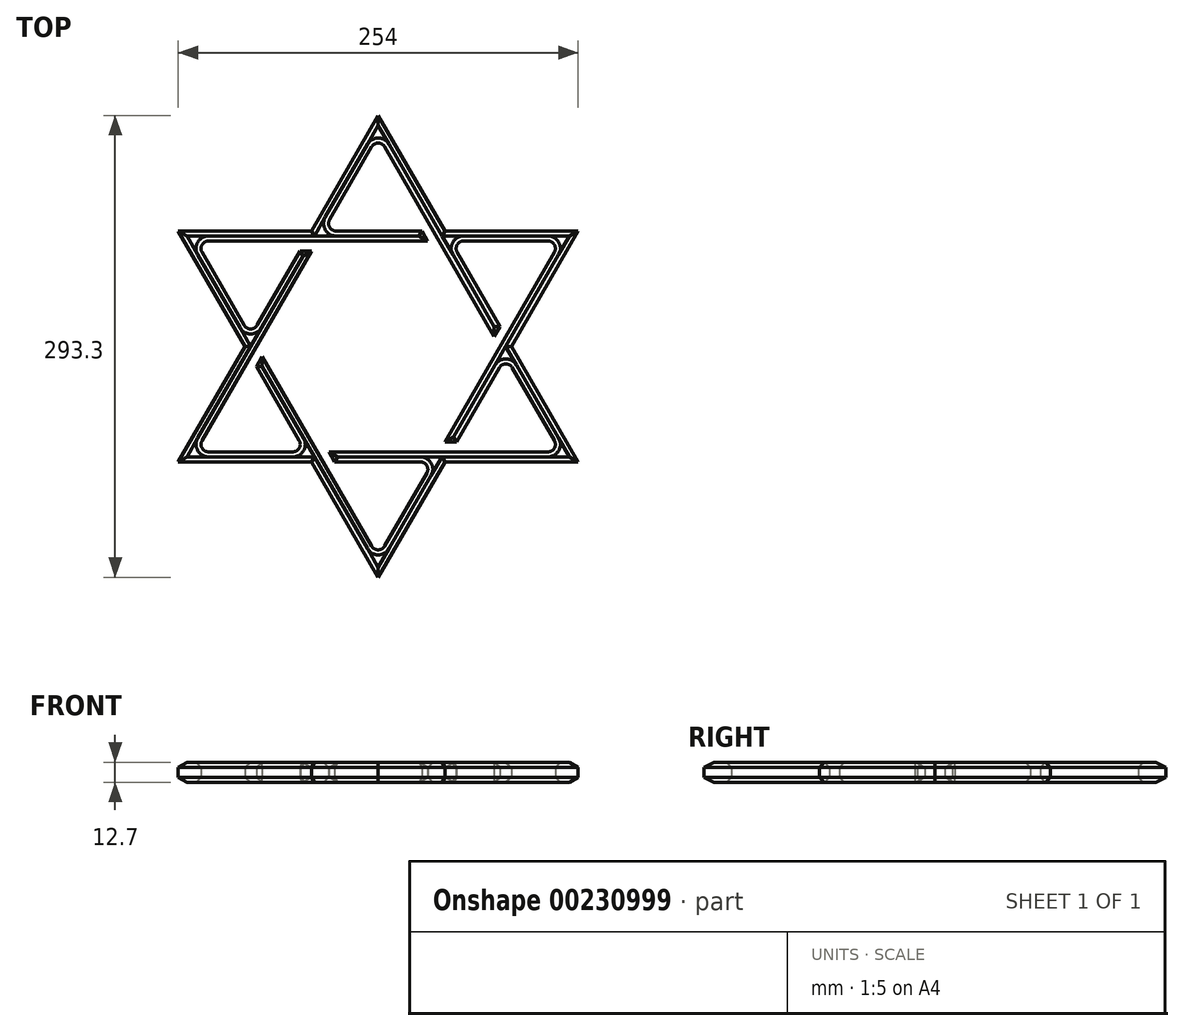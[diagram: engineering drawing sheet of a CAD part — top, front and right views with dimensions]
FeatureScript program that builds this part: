
annotation { "Feature Type Name" : "Feature", "Feature Type Description" : "" }
export const myFeature = defineFeature(function(context is Context, id is Id, definition is map)
    precondition{}
    {
        {
            var Q0;
            Q0=qCreatedBy(makeId("Top.planeOp"),FACE);
            var sketch = newSketch(context, id + "F0", { "sketchPlane" : qUnion([Q0])});
            skLineSegment(sketch, "E0", {"start": v(0, 146.65) * mm, "end": v(-42.33, 73.32) * mm});
            skLineSegment(sketch, "E1", {"start": v(-127, -73.32) * mm, "end": v(-42.33, -73.32) * mm});
            skLineSegment(sketch, "E2", {"start": v(0, 146.65) * mm, "end": v(42.33, 73.32) * mm});
            skLineSegment(sketch, "E3", {"start": v(127, 73.32) * mm, "end": v(84.67, 0) * mm});
            skLineSegment(sketch, "E4", {"start": v(0, -146.65) * mm, "end": v(-42.33, -73.32) * mm});
            skLineSegment(sketch, "E5", {"start": v(127, 73.32) * mm, "end": v(42.33, 73.32) * mm});
            skLineSegment(sketch, "E6.0", {"start": v(111.88, 59.83) * mm, "end": v(42.33, -60.62) * mm});
            skLineSegment(sketch, "E7.0", {"start": v(107.75, 66.97) * mm, "end": v(54.25, 66.97) * mm});
            skLineSegment(sketch, "E8.0", {"start": v(-4.12, -126.8) * mm, "end": v(-73.67, -6.35) * mm});
            skLineSegment(sketch, "E9.trimOffspring", {"start": v(-4.12, 126.8) * mm, "end": v(-30.88, 80.47) * mm});
            skLineSegment(sketch, "E10.trimOffspring", {"start": v(4.12, 126.8) * mm, "end": v(73.67, 6.35) * mm});
            skLineSegment(sketch, "E11.trimOffspring", {"start": v(-107.75, -66.97) * mm, "end": v(-54.25, -66.97) * mm});
            skLineSegment(sketch, "E12.0", {"start": v(-27.67, -73.32) * mm, "end": v(-31.33, -66.97) * mm});
            skLineSegment(sketch, "E13.trimOffspring", {"start": v(31.33, 66.97) * mm, "end": v(-107.75, 66.97) * mm});
            skLineSegment(sketch, "E14.trimOffspring", {"start": v(27.67, 73.32) * mm, "end": v(-26.75, 73.32) * mm});
            skLineSegment(sketch, "E15.trimOffspring", {"start": v(84.67, 0) * mm, "end": v(127, -73.32) * mm});
            skLineSegment(sketch, "E16.trimOffspring", {"start": v(77.33, 12.7) * mm, "end": v(73.67, 6.35) * mm});
            skLineSegment(sketch, "E17.trimOffspring", {"start": v(85.12, -13.5) * mm, "end": v(111.88, -59.83) * mm});
            skLineSegment(sketch, "E18.trimOffspring", {"start": v(42.33, -73.32) * mm, "end": v(0, -146.65) * mm});
            skLineSegment(sketch, "E19.trimOffspring", {"start": v(30.88, -80.47) * mm, "end": v(4.12, -126.8) * mm});
            skLineSegment(sketch, "E20.trimOffspring", {"start": v(42.33, -60.62) * mm, "end": v(49.67, -60.62) * mm});
            skLineSegment(sketch, "E21.trimOffspring", {"start": v(-27.67, -73.32) * mm, "end": v(26.75, -73.32) * mm});
            skLineSegment(sketch, "E22.trimOffspring", {"start": v(-31.33, -66.97) * mm, "end": v(107.75, -66.97) * mm});
            skLineSegment(sketch, "E23.trimOffspring", {"start": v(-84.67, 0) * mm, "end": v(-127, 73.32) * mm});
            skLineSegment(sketch, "E24.trimOffspring", {"start": v(-85.12, 13.5) * mm, "end": v(-111.88, 59.83) * mm});
            skLineSegment(sketch, "E25.trimOffspring", {"start": v(-73.67, -6.35) * mm, "end": v(-77.33, -12.7) * mm});
            skLineSegment(sketch, "E26.trimOffspring", {"start": v(-42.33, 60.62) * mm, "end": v(-111.88, -59.83) * mm});
            skLineSegment(sketch, "E27.trimOffspring", {"start": v(-49.67, 60.62) * mm, "end": v(-76.88, 13.5) * mm});
            skLineSegment(sketch, "E28.trimOffspring", {"start": v(-42.33, 60.62) * mm, "end": v(-49.67, 60.62) * mm});
            skLineSegment(sketch, "E29.trimOffspring", {"start": v(27.67, 73.32) * mm, "end": v(31.33, 66.97) * mm});
            skLineSegment(sketch, "E30.trimOffspring", {"start": v(-42.33, 73.32) * mm, "end": v(-127, 73.32) * mm});
            skLineSegment(sketch, "E31.trimOffspring", {"start": v(50.12, 59.83) * mm, "end": v(77.33, 12.7) * mm});
            skLineSegment(sketch, "E32.trimOffspring", {"start": v(76.88, -13.5) * mm, "end": v(49.67, -60.62) * mm});
            skLineSegment(sketch, "E33.trimOffspring", {"start": v(42.33, -73.32) * mm, "end": v(127, -73.32) * mm});
            skLineSegment(sketch, "E34.trimOffspring", {"start": v(-84.67, 0) * mm, "end": v(-127, -73.32) * mm});
            skLineSegment(sketch, "E35.trimOffspring", {"start": v(-50.12, -59.83) * mm, "end": v(-77.33, -12.7) * mm});
            skPoint(sketch, "E36.visualSharp", {"position": v(-116, 66.97) * mm});
            skArc(sketch, "E36.filletArc", {"start": v(-107.75, 66.97) * mm, "mid": v(-111.88, 64.6) * mm, "end": v(-111.88, 59.83) * mm});
            skPoint(sketch, "E37.visualSharp", {"position": v(0, 133.95) * mm});
            skArc(sketch, "E37.filletArc", {"start": v(4.12, 126.8) * mm, "mid": v(0, 129.18) * mm, "end": v(-4.12, 126.8) * mm});
            skPoint(sketch, "E38.visualSharp", {"position": v(-35, 73.32) * mm});
            skArc(sketch, "E38.filletArc", {"start": v(-30.88, 80.47) * mm, "mid": v(-30.88, 75.7) * mm, "end": v(-26.75, 73.32) * mm});
            skPoint(sketch, "E39.visualSharp", {"position": v(46, 66.97) * mm});
            skArc(sketch, "E39.filletArc", {"start": v(54.25, 66.97) * mm, "mid": v(50.12, 64.6) * mm, "end": v(50.12, 59.83) * mm});
            skPoint(sketch, "E40.visualSharp", {"position": v(116, 66.97) * mm});
            skArc(sketch, "E40.filletArc", {"start": v(111.88, 59.83) * mm, "mid": v(111.88, 64.6) * mm, "end": v(107.75, 66.97) * mm});
            skPoint(sketch, "E41.visualSharp", {"position": v(116, -66.97) * mm});
            skArc(sketch, "E41.filletArc", {"start": v(107.75, -66.97) * mm, "mid": v(111.88, -64.6) * mm, "end": v(111.88, -59.83) * mm});
            skPoint(sketch, "E42.visualSharp", {"position": v(81, -6.35) * mm});
            skArc(sketch, "E42.filletArc", {"start": v(85.12, -13.5) * mm, "mid": v(81, -11.11) * mm, "end": v(76.88, -13.5) * mm});
            skPoint(sketch, "E43.visualSharp", {"position": v(0, -133.95) * mm});
            skArc(sketch, "E43.filletArc", {"start": v(-4.12, -126.8) * mm, "mid": v(0, -129.18) * mm, "end": v(4.12, -126.8) * mm});
            skPoint(sketch, "E44.visualSharp", {"position": v(35, -73.32) * mm});
            skArc(sketch, "E44.filletArc", {"start": v(30.88, -80.47) * mm, "mid": v(30.88, -75.7) * mm, "end": v(26.75, -73.32) * mm});
            skPoint(sketch, "E45.visualSharp", {"position": v(-116, -66.97) * mm});
            skArc(sketch, "E45.filletArc", {"start": v(-111.88, -59.83) * mm, "mid": v(-111.88, -64.6) * mm, "end": v(-107.75, -66.97) * mm});
            skPoint(sketch, "E46.visualSharp", {"position": v(-81, 6.35) * mm});
            skArc(sketch, "E46.filletArc", {"start": v(-85.12, 13.5) * mm, "mid": v(-81, 11.11) * mm, "end": v(-76.88, 13.5) * mm});
            skPoint(sketch, "E47.visualSharp", {"position": v(-46, -66.97) * mm});
            skArc(sketch, "E47.filletArc", {"start": v(-54.25, -66.97) * mm, "mid": v(-50.12, -64.6) * mm, "end": v(-50.12, -59.83) * mm});
            skSolve(sketch);
        }
        {
            var Q0;
            Q0=makeQuery(id+"F0.imprint","IMPRINT",FACE,{"disambiguationData":[TD([[makeQuery(id+"F0.imprint","IMPRINT",EDGE,{"derivedFrom":sQuery(id+"F0.wireOp",EDGE,"E0")}),1.0]])]});
            extrude(context, id + "F1", {"entities" : qUnion([Q0]), "depth" : 12.7 * mm});
        }
        {
            var Q0;
            Q0=makeQuery(id+"F1.opExtrude","CAP_FACE",FACE,{"disambiguationData":[OSD([sQuery(id+"F0.wireOp",EDGE,"E0"),sQuery(id+"F0.wireOp",EDGE,"E1"),sQuery(id+"F0.wireOp",EDGE,"E2"),sQuery(id+"F0.wireOp",EDGE,"E3"),sQuery(id+"F0.wireOp",EDGE,"E4"),sQuery(id+"F0.wireOp",EDGE,"E5"),sQuery(id+"F0.wireOp",EDGE,"E6.0"),sQuery(id+"F0.wireOp",EDGE,"E7.0"),sQuery(id+"F0.wireOp",EDGE,"E8.0"),sQuery(id+"F0.wireOp",EDGE,"E9.trimOffspring"),sQuery(id+"F0.wireOp",EDGE,"E10.trimOffspring"),sQuery(id+"F0.wireOp",EDGE,"E11.trimOffspring"),sQuery(id+"F0.wireOp",EDGE,"E12.0"),sQuery(id+"F0.wireOp",EDGE,"E13.trimOffspring"),sQuery(id+"F0.wireOp",EDGE,"E14.trimOffspring"),sQuery(id+"F0.wireOp",EDGE,"E15.trimOffspring"),sQuery(id+"F0.wireOp",EDGE,"E16.trimOffspring"),sQuery(id+"F0.wireOp",EDGE,"E17.trimOffspring"),sQuery(id+"F0.wireOp",EDGE,"E18.trimOffspring"),sQuery(id+"F0.wireOp",EDGE,"E19.trimOffspring"),sQuery(id+"F0.wireOp",EDGE,"E20.trimOffspring"),sQuery(id+"F0.wireOp",EDGE,"E21.trimOffspring"),sQuery(id+"F0.wireOp",EDGE,"E22.trimOffspring"),sQuery(id+"F0.wireOp",EDGE,"E23.trimOffspring"),sQuery(id+"F0.wireOp",EDGE,"E24.trimOffspring"),sQuery(id+"F0.wireOp",EDGE,"E25.trimOffspring"),sQuery(id+"F0.wireOp",EDGE,"E26.trimOffspring"),sQuery(id+"F0.wireOp",EDGE,"E27.trimOffspring"),sQuery(id+"F0.wireOp",EDGE,"E28.trimOffspring"),sQuery(id+"F0.wireOp",EDGE,"E29.trimOffspring"),sQuery(id+"F0.wireOp",EDGE,"E30.trimOffspring"),sQuery(id+"F0.wireOp",EDGE,"E31.trimOffspring"),sQuery(id+"F0.wireOp",EDGE,"E32.trimOffspring"),sQuery(id+"F0.wireOp",EDGE,"E33.trimOffspring"),sQuery(id+"F0.wireOp",EDGE,"E34.trimOffspring"),sQuery(id+"F0.wireOp",EDGE,"E35.trimOffspring"),sQuery(id+"F0.wireOp",EDGE,"E36.filletArc"),sQuery(id+"F0.wireOp",EDGE,"E37.filletArc"),sQuery(id+"F0.wireOp",EDGE,"E38.filletArc"),sQuery(id+"F0.wireOp",EDGE,"E39.filletArc"),sQuery(id+"F0.wireOp",EDGE,"E40.filletArc"),sQuery(id+"F0.wireOp",EDGE,"E41.filletArc"),sQuery(id+"F0.wireOp",EDGE,"E42.filletArc"),sQuery(id+"F0.wireOp",EDGE,"E43.filletArc"),sQuery(id+"F0.wireOp",EDGE,"E44.filletArc"),sQuery(id+"F0.wireOp",EDGE,"E45.filletArc"),sQuery(id+"F0.wireOp",EDGE,"E46.filletArc"),sQuery(id+"F0.wireOp",EDGE,"E47.filletArc")])],"isStart":false});
            chamfer(context, id + "F2", {"entities" : qUnion([Q0]), "width" : 3.17 * mm, "tangentPropagation" : true});
        }
        {
            var Q0;
            Q0=makeQuery(id+"F1.opExtrude","CAP_FACE",FACE,{"disambiguationData":[OSD([sQuery(id+"F0.wireOp",EDGE,"E0"),sQuery(id+"F0.wireOp",EDGE,"E1"),sQuery(id+"F0.wireOp",EDGE,"E2"),sQuery(id+"F0.wireOp",EDGE,"E3"),sQuery(id+"F0.wireOp",EDGE,"E4"),sQuery(id+"F0.wireOp",EDGE,"E5"),sQuery(id+"F0.wireOp",EDGE,"E6.0"),sQuery(id+"F0.wireOp",EDGE,"E7.0"),sQuery(id+"F0.wireOp",EDGE,"E8.0"),sQuery(id+"F0.wireOp",EDGE,"E9.trimOffspring"),sQuery(id+"F0.wireOp",EDGE,"E10.trimOffspring"),sQuery(id+"F0.wireOp",EDGE,"E11.trimOffspring"),sQuery(id+"F0.wireOp",EDGE,"E12.0"),sQuery(id+"F0.wireOp",EDGE,"E13.trimOffspring"),sQuery(id+"F0.wireOp",EDGE,"E14.trimOffspring"),sQuery(id+"F0.wireOp",EDGE,"E15.trimOffspring"),sQuery(id+"F0.wireOp",EDGE,"E16.trimOffspring"),sQuery(id+"F0.wireOp",EDGE,"E17.trimOffspring"),sQuery(id+"F0.wireOp",EDGE,"E18.trimOffspring"),sQuery(id+"F0.wireOp",EDGE,"E19.trimOffspring"),sQuery(id+"F0.wireOp",EDGE,"E20.trimOffspring"),sQuery(id+"F0.wireOp",EDGE,"E21.trimOffspring"),sQuery(id+"F0.wireOp",EDGE,"E22.trimOffspring"),sQuery(id+"F0.wireOp",EDGE,"E23.trimOffspring"),sQuery(id+"F0.wireOp",EDGE,"E24.trimOffspring"),sQuery(id+"F0.wireOp",EDGE,"E25.trimOffspring"),sQuery(id+"F0.wireOp",EDGE,"E26.trimOffspring"),sQuery(id+"F0.wireOp",EDGE,"E27.trimOffspring"),sQuery(id+"F0.wireOp",EDGE,"E28.trimOffspring"),sQuery(id+"F0.wireOp",EDGE,"E29.trimOffspring"),sQuery(id+"F0.wireOp",EDGE,"E30.trimOffspring"),sQuery(id+"F0.wireOp",EDGE,"E31.trimOffspring"),sQuery(id+"F0.wireOp",EDGE,"E32.trimOffspring"),sQuery(id+"F0.wireOp",EDGE,"E33.trimOffspring"),sQuery(id+"F0.wireOp",EDGE,"E34.trimOffspring"),sQuery(id+"F0.wireOp",EDGE,"E35.trimOffspring"),sQuery(id+"F0.wireOp",EDGE,"E36.filletArc"),sQuery(id+"F0.wireOp",EDGE,"E37.filletArc"),sQuery(id+"F0.wireOp",EDGE,"E38.filletArc"),sQuery(id+"F0.wireOp",EDGE,"E39.filletArc"),sQuery(id+"F0.wireOp",EDGE,"E40.filletArc"),sQuery(id+"F0.wireOp",EDGE,"E41.filletArc"),sQuery(id+"F0.wireOp",EDGE,"E42.filletArc"),sQuery(id+"F0.wireOp",EDGE,"E43.filletArc"),sQuery(id+"F0.wireOp",EDGE,"E44.filletArc"),sQuery(id+"F0.wireOp",EDGE,"E45.filletArc"),sQuery(id+"F0.wireOp",EDGE,"E46.filletArc"),sQuery(id+"F0.wireOp",EDGE,"E47.filletArc")])],"isStart":true});
            chamfer(context, id + "F3", {"entities" : qUnion([Q0]), "width" : 3.17 * mm, "tangentPropagation" : true});
        }
    });
